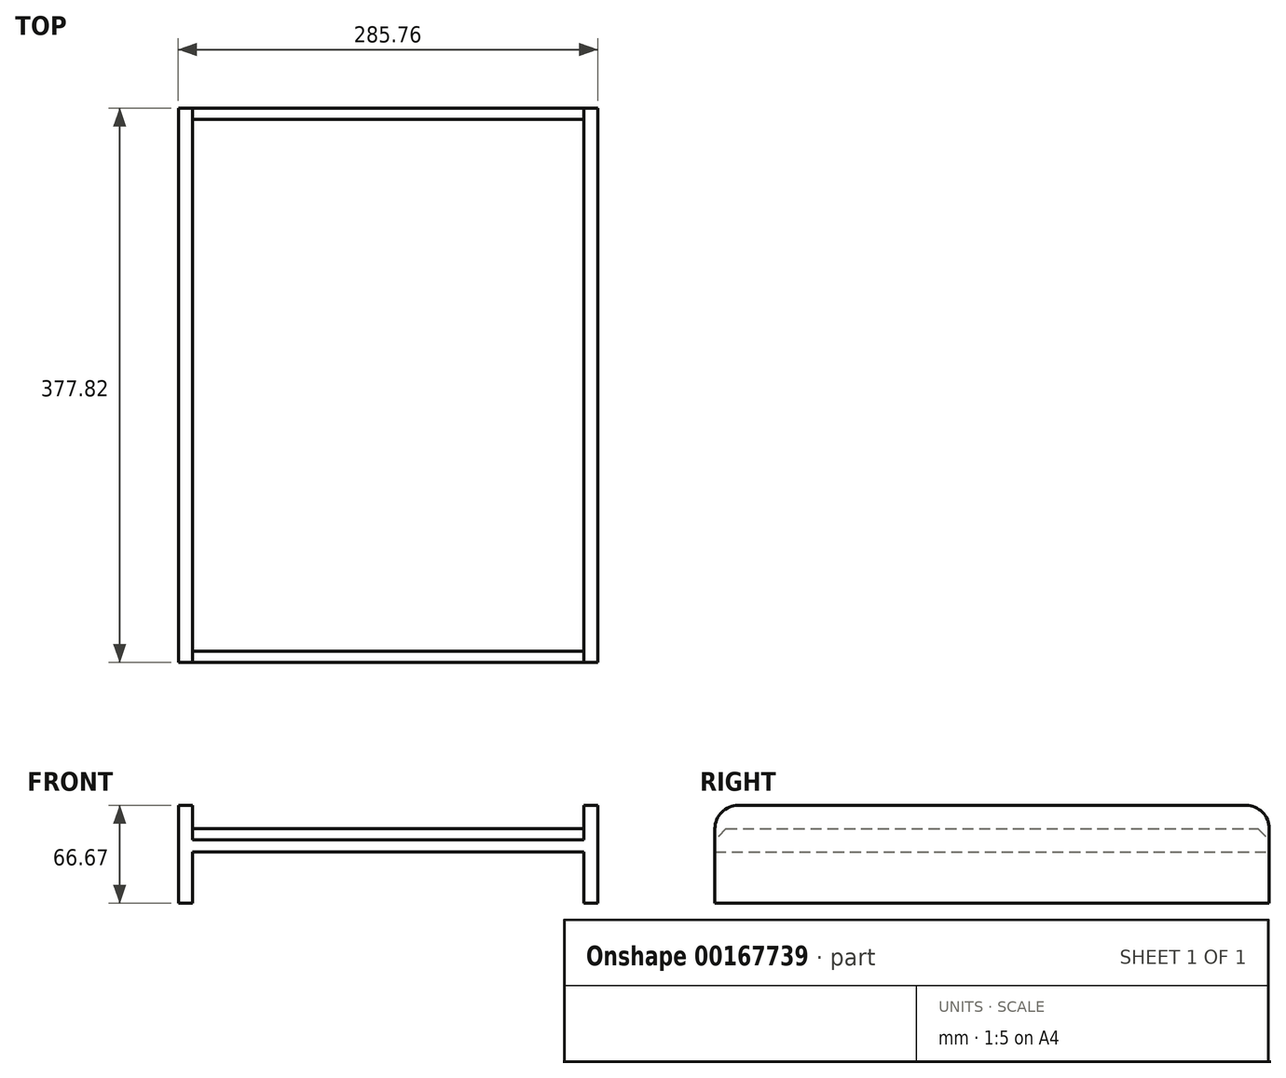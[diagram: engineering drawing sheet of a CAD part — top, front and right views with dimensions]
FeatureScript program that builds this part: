
annotation { "Feature Type Name" : "Feature", "Feature Type Description" : "" }
export const myFeature = defineFeature(function(context is Context, id is Id, definition is map)
    precondition{}
    {
        {
            var Q0;
            Q0=qCreatedBy(makeId("Front.planeOp"),FACE);
            var sketch = newSketch(context, id + "F0", { "sketchPlane" : qUnion([Q0])});
            skLineSegment(sketch, "E0.bottom", {"start": v(133.35, 7.94) * mm, "end": v(-133.35, 7.94) * mm});
            skLineSegment(sketch, "E0.top", {"start": v(133.35, -7.94) * mm, "end": v(-133.35, -7.94) * mm});
            skLineSegment(sketch, "E0.left", {"start": v(133.35, 7.94) * mm, "end": v(133.35, -7.94) * mm});
            skLineSegment(sketch, "E0.right", {"start": v(-133.35, 7.94) * mm, "end": v(-133.35, -7.94) * mm});
            skPoint(sketch, "E0.middle", {"position": v(0, 0) * mm});
            skLineSegment(sketch, "E1", {"start": v(133.35, 7.94) * mm, "end": v(133.35, 23.81) * mm});
            skLineSegment(sketch, "E2", {"start": v(133.35, 23.81) * mm, "end": v(142.88, 23.81) * mm});
            skLineSegment(sketch, "E3", {"start": v(142.88, 23.81) * mm, "end": v(142.88, -42.86) * mm});
            skLineSegment(sketch, "E4", {"start": v(142.88, -42.86) * mm, "end": v(133.35, -42.86) * mm});
            skLineSegment(sketch, "E5", {"start": v(133.35, -42.86) * mm, "end": v(133.35, 7.94) * mm});
            skLineSegment(sketch, "E6.MirrorCS", {"start": v(-133.35, 7.94) * mm, "end": v(-133.35, 23.81) * mm});
            skLineSegment(sketch, "E7.MirrorCS", {"start": v(-133.35, 23.81) * mm, "end": v(-142.88, 23.81) * mm});
            skLineSegment(sketch, "E8.MirrorCS", {"start": v(-142.88, 23.81) * mm, "end": v(-142.88, -42.86) * mm});
            skLineSegment(sketch, "E9.MirrorCS", {"start": v(-142.88, -42.86) * mm, "end": v(-133.35, -42.86) * mm});
            skLineSegment(sketch, "E10.MirrorCS", {"start": v(-133.35, -42.86) * mm, "end": v(-133.35, 7.94) * mm});
            skSolve(sketch);
        }
        {
            var Q0;
            Q0 = qSketchRegion(id + "F0", true);
            extrude(context, id + "F1", {"entities" : qUnion([Q0]), "endBound" : BoundingType.SYMMETRIC, "depth" : 377.82 * mm});
        }
        {
            var Q0;
            Q0=makeQuery(id+"F1.opExtrude","CAP_EDGE",EDGE,{"disambiguationData":[OSD([sQuery(id+"F0.wireOp",EDGE,"E7.MirrorCS")])],"isStart":false});
            var Q1;
            Q1=makeQuery(id+"F1.opExtrude","CAP_EDGE",EDGE,{"disambiguationData":[OSD([sQuery(id+"F0.wireOp",EDGE,"E7.MirrorCS")])],"isStart":true});
            var Q2;
            Q2=makeQuery(id+"F1.opExtrude","CAP_EDGE",EDGE,{"disambiguationData":[OSD([sQuery(id+"F0.wireOp",EDGE,"E2")])],"isStart":true});
            var Q3;
            Q3=makeQuery(id+"F1.opExtrude","CAP_EDGE",EDGE,{"disambiguationData":[OSD([sQuery(id+"F0.wireOp",EDGE,"E2")])],"isStart":false});
            fillet(context, id + "F2", {"entities" : qUnion([Q0, Q1, Q2, Q3]), "radius" : 15.88 * mm, "tangentPropagation" : true, "allowEdgeOverflow" : false});
        }
        {
            var Q0;
            Q0=makeQuery(id+"F1.opExtrude","CAP_EDGE",EDGE,{"disambiguationData":[OSD([sQuery(id+"F0.wireOp",EDGE,"E0.bottom")])],"isStart":false});
            var Q1;
            Q1=makeQuery(id+"F1.opExtrude","CAP_EDGE",EDGE,{"disambiguationData":[OSD([sQuery(id+"F0.wireOp",EDGE,"E0.bottom")])],"isStart":true});
            chamfer(context, id + "F3", {"entities" : qUnion([Q0, Q1]), "width" : 7.62 * mm, "tangentPropagation" : true});
        }
    });
